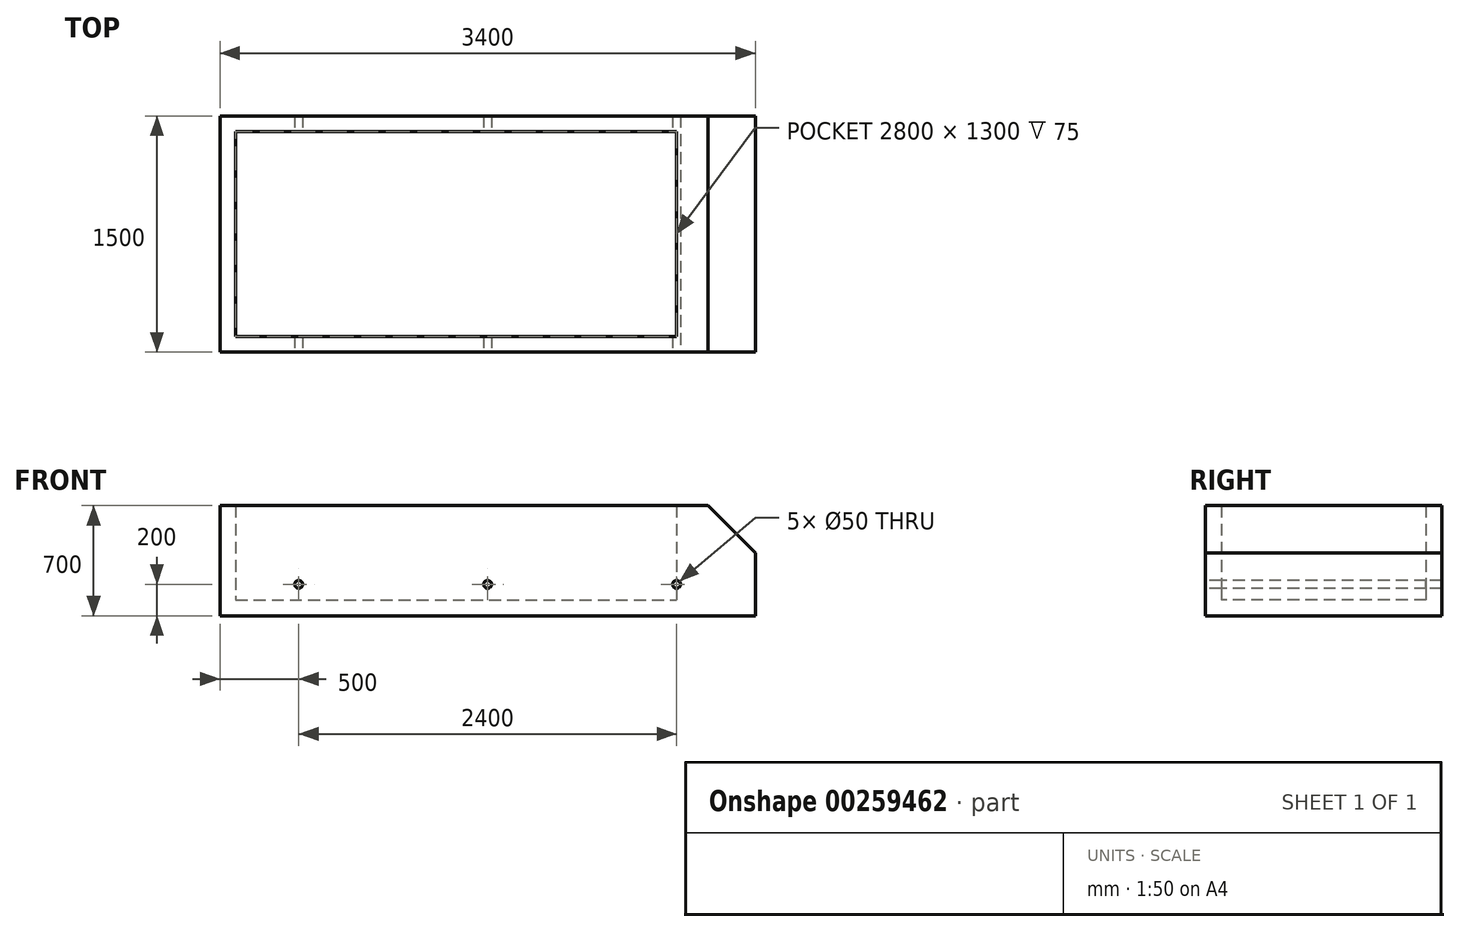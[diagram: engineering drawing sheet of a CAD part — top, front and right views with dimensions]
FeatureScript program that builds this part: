
annotation { "Feature Type Name" : "Feature", "Feature Type Description" : "" }
export const myFeature = defineFeature(function(context is Context, id is Id, definition is map)
    precondition{}
    {
        {
            var Q0;
            Q0=qCreatedBy(makeId("Top.planeOp"),FACE);
            var sketch = newSketch(context, id + "F0", { "sketchPlane" : qUnion([Q0])});
            skLineSegment(sketch, "E0.bottom", {"start": v(-1500, 750) * mm, "end": v(1500, 750) * mm});
            skLineSegment(sketch, "E0.top", {"start": v(-1500, -750) * mm, "end": v(1500, -750) * mm});
            skLineSegment(sketch, "E0.left", {"start": v(-1500, 750) * mm, "end": v(-1500, -750) * mm});
            skLineSegment(sketch, "E0.right", {"start": v(1500, 750) * mm, "end": v(1500, -750) * mm});
            skSolve(sketch);
        }
        {
            var Q0;
            Q0=makeQuery(id+"F0.imprint","IMPRINT",FACE,{"disambiguationData":[TD([[makeQuery(id+"F0.imprint","IMPRINT",EDGE,{"derivedFrom":sQuery(id+"F0.wireOp",EDGE,"E0.bottom")}),-1.0]])]});
            extrude(context, id + "F1", {"entities" : qUnion([Q0]), "depth" : 700 * mm});
        }
        {
            var Q0;
            Q0=makeQuery(id+"F1.opExtrude","CAP_FACE",FACE,{"disambiguationData":[OSD([sQuery(id+"F0.wireOp",EDGE,"E0.bottom"),sQuery(id+"F0.wireOp",EDGE,"E0.top"),sQuery(id+"F0.wireOp",EDGE,"E0.left"),sQuery(id+"F0.wireOp",EDGE,"E0.right")])],"isStart":false});
            shell(context, id + "F2", {"entities" : qUnion([Q0]), "thickness" : 100 * mm});
        }
        {
            var Q0;
            Q0=makeQuery(id+"F1.opExtrude","SWEPT_FACE",FACE,{"disambiguationData":[OSD([sQuery(id+"F0.wireOp",EDGE,"E0.right")])]});
            extrude(context, id + "F3", {"entities" : qUnion([Q0]), "operationType" : NewBodyOperationType.ADD, "depth" : 400 * mm});
        }
        {
            var Q0;
            {var subQ0=sQuery(id+"F0.wireOp",EDGE,"E0.right");Q0=makeQuery(id+"F3.opExtrude","CAP_EDGE",EDGE,{"disambiguationData":[OSD([subQ0]),TDD([makeQuery(id+"F1.opExtrude","CAP_EDGE",EDGE,{"disambiguationData":[OSD([subQ0])],"isStart":false})])],"isStart":false});}
            chamfer(context, id + "F4", {"entities" : qUnion([Q0]), "width" : 300 * mm, "tangentPropagation" : true});
        }
        {
            var Q0;
            {var subQ0=sQuery(id+"F0.wireOp",EDGE,"E0.top");Q0=makeQuery(id+"F3.boolean.opBoolean","MERGE",FACE,{"derivedFrom":[makeQuery(id+"F1.opExtrude","SWEPT_FACE",FACE,{"disambiguationData":[OSD([subQ0])]}),makeQuery(id+"F3.opExtrude","SWEPT_FACE",FACE,{"disambiguationData":[OSD([subQ0,sQuery(id+"F0.wireOp",EDGE,"E0.right")])]})]});}
            var sketch = newSketch(context, id + "F5", { "sketchPlane" : qUnion([Q0])});
            skPoint(sketch, "E1", {"position": v(1400, 200) * mm});
            skPoint(sketch, "E1.positionSnap0", {"position": v(1900, 200) * mm});
            skPoint(sketch, "E2", {"position": v(200, 200) * mm});
            skPoint(sketch, "E3", {"position": v(-1000, 200) * mm});
            skSolve(sketch);
        }
        {
            var Q0;
            Q0=sQuery(id+"F5.wireOp",VERTEX,"E2");
            var Q1;
            Q1=sQuery(id+"F5.wireOp",VERTEX,"E3");
            var Q2;
            Q2=sQuery(id+"F5.wireOp",VERTEX,"E1");
            var Q3;
            Q3=makeQuery(id+"F1.opExtrude","SWEPT_BODY",BODY,{"disambiguationData":[OSD([sQuery(id+"F0.wireOp",EDGE,"E0.bottom"),sQuery(id+"F0.wireOp",EDGE,"E0.top"),sQuery(id+"F0.wireOp",EDGE,"E0.left"),sQuery(id+"F0.wireOp",EDGE,"E0.right")])]});
            hole(context, id + "F6", {"style" : HoleStyle.SIMPLE, "endStyle" : HoleEndStyle.THROUGH, "holeDiameter" : 50 * mm, "tappedDepth" : 12 * mm, "tapClearance" : 3, "startFromSketch" : true, "locations" : qUnion([Q0, Q1, Q2]), "scope" : qUnion([Q3])});
        }
    });
